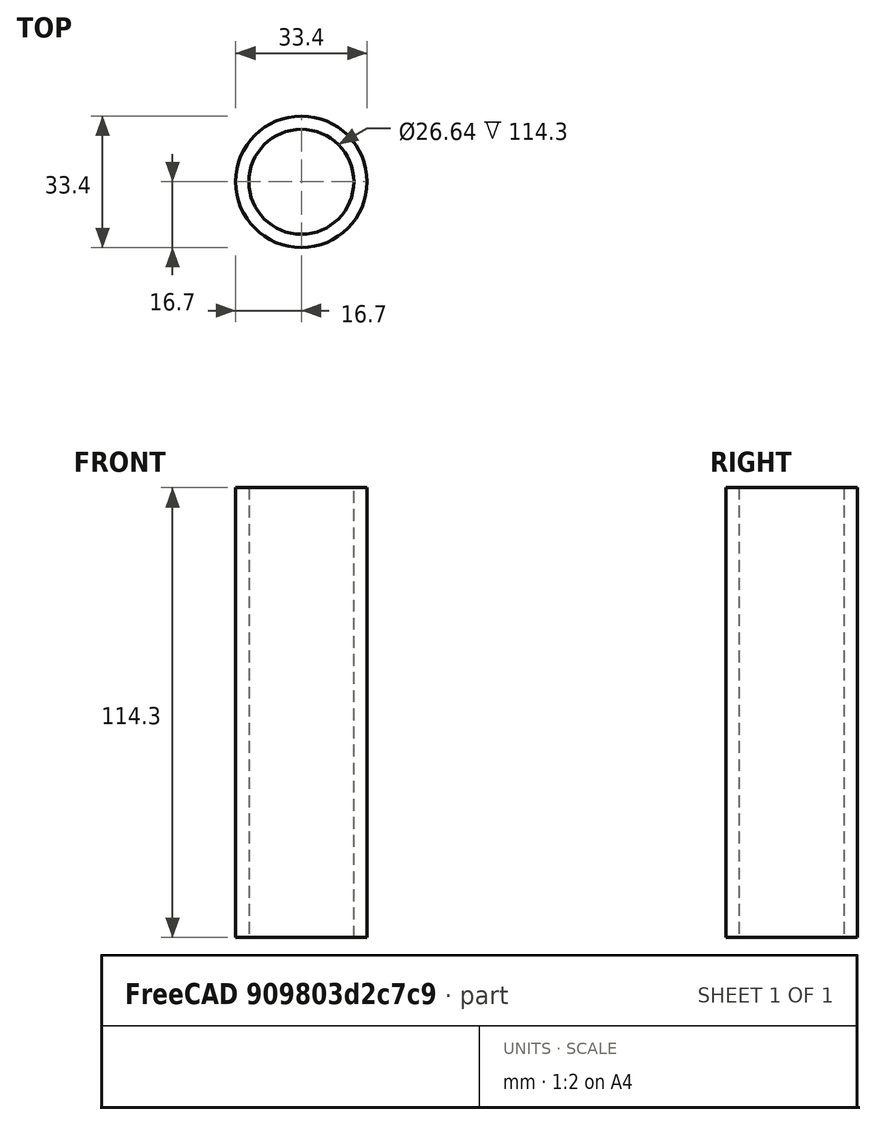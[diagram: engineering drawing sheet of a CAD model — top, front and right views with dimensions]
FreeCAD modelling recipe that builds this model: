
FCSTD DOCUMENT  (FreeCAD 0.20R29410 (Git))
Label: PipeNipple
License: All rights reserved
LicenseURL: http://en.wikipedia.org/wiki/All_rights_reserved
objects: PartDesign::CoordinateSystem×2, Sketcher::SketchObject×1, PartDesign::Pad×1, PartDesign::Body×1
note: 6 computed .brp shape members not serialized (recipe doc carries the construction recipe); baked Part::Feature solids carry a one-line shape summary decoded from their .brp

FEATURE [Sketcher::SketchObject] Sketch
  FullyConstrained = true
  MapMode = 5
  Support = -> [XY_Plane]
  sketch-geometry (2):
    g0: Circle CenterX=0 CenterY=0 CenterZ=0 NormalX=0 NormalY=0 NormalZ=1 AngleXU=0 Radius=13.3223
    g1: Circle CenterX=0 CenterY=0 CenterZ=0 NormalX=0 NormalY=0 NormalZ=1 AngleXU=0 Radius=16.7005
  constraints (4):
    c: Coincident(g0,g-1)
    c: Coincident(g1,g0)
    c: Diameter(g1) = 33.401
    c: Diameter(g0) = 26.6446
FEATURE [PartDesign::Pad] Pad
  Direction = (0,0,1)
  Length = 114.3
  Length2 = 10
  Profile = -> Sketch
  ReferenceAxis = -> Sketch [N_Axis]
  Type = 0
FEATURE [PartDesign::CoordinateSystem] LCS_root
  AttacherType = Attacher::AttachEngine3D
  MapMode = 2
  Support = -> [XY_Plane]
FEATURE [PartDesign::CoordinateSystem] LCS_end
  AttacherType = Attacher::AttachEngine3D
  AttachmentOffset = pos=(0,0,114.3) rot=(0,0,1;0rad)
  MapMode = 2
  Placement = pos=(0,0,114.3) rot=(0,0,1;0rad)
  Support = -> [LCS_root]
  expr: .AttachmentOffset.Base.z = <<Pad>>.Length
FEATURE [PartDesign::Body] Body
  Group = -> [Sketch,Pad,LCS_root,LCS_end]
  Origin = -> Origin
  Tip = -> Pad
